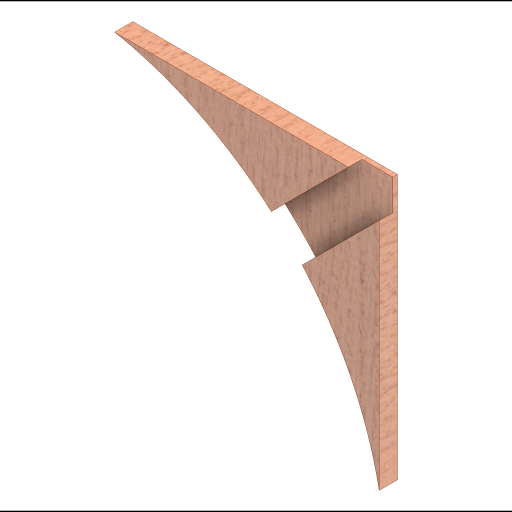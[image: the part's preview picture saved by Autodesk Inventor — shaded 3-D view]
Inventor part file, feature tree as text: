
AUTODESK INVENTOR PART (.ipt)
format: ipt  version: 2023 (Build 270158000, 158)  size: 205,312 bytes
history: native  units: in
note: dims shown in document units (in); Inventor stores cm internally (conversion verified against a paired STEP export)
features: extrude x4, sketch x4, projected_geometry x1
ambient origin geometry x8: Origin, YZ Plane, XZ Plane, XY Plane, X Axis, Y Axis, Z Axis, Center Point
bodies: Solid1 (feature_tree)
feature tree (9):
  extrude  "Extrusion1"  Depth=17.0in
  extrude  "Extrusion2"  Depth=8.5in
  extrude  "Extrusion3"  Depth=0.47in TaperAngle=0.0deg
  extrude  "Extrusion5"  TaperAngle=0.0deg  [1 undecoded]
  sketch  "Sketch1"  dims[d0=17.0in d1=17.0in]
  sketch  "Sketch2"  dims[d2=17.0in d3=8.5in]
  sketch  "Sketch3"  dims[d4=8.5in d5=0.47in d6=0.0in]
  sketch  "Sketch5"  dims[d7=17.3228in d8=0.0in d9=0.0in d10=1.0in d11=135.0deg d12=135.0deg d13=0.707in d14=90.0deg d15=5.0in d16=0.35in d17=0.0in d22=90.0deg d25=0.0297in d26=0.063in d27=0.063in d28=1.063in d29=0.0in]
  projected_geometry  "Projected Loop2"
note: 1 required parameter value undecoded (feature->parameter linkage not recoverable at this tier; creation-order binding heuristic only, values carry confidence <= 0.55)
